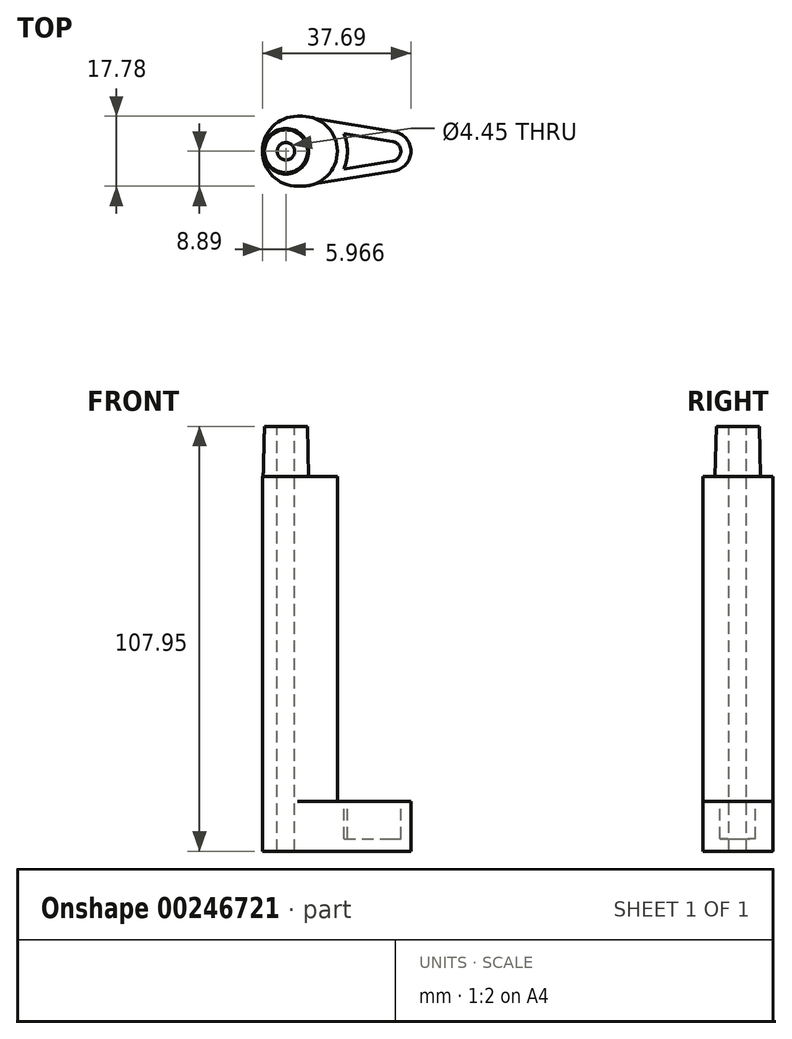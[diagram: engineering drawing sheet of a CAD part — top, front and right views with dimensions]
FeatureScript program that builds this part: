
annotation { "Feature Type Name" : "Feature", "Feature Type Description" : "" }
export const myFeature = defineFeature(function(context is Context, id is Id, definition is map)
    precondition{}
    {
        {
            var Q0;
            Q0=qCreatedBy(makeId("Top.planeOp"),FACE);
            var sketch = newSketch(context, id + "F0", { "sketchPlane" : qUnion([Q0])});
            skArc(sketch, "E0", {"start": v(-9.14, 8.77) * mm, "mid": v(-19.45, 0) * mm, "end": v(-9.14, -8.77) * mm});
            skArc(sketch, "E1", {"start": v(13.98, -5.01) * mm, "mid": v(18.24, 0) * mm, "end": v(13.98, 5.01) * mm});
            skLineSegment(sketch, "E2", {"start": v(-9.14, 8.77) * mm, "end": v(13.98, 5.01) * mm});
            skLineSegment(sketch, "E3", {"start": v(13.98, -5.01) * mm, "end": v(-9.14, -8.77) * mm});
            skSolve(sketch);
        }
        {
            var Q0;
            Q0=makeQuery(id+"F0.imprint","IMPRINT",FACE,{"disambiguationData":[TD([[makeQuery(id+"F0.imprint","IMPRINT",EDGE,{"derivedFrom":sQuery(id+"F0.wireOp",EDGE,"E0")}),1.0]])]});
            extrude(context, id + "F1", {"entities" : qUnion([Q0]), "depth" : 12.7 * mm});
        }
        {
            var Q0;
            Q0=makeQuery(id+"F1.opExtrude","CAP_FACE",FACE,{"disambiguationData":[OSD([sQuery(id+"F0.wireOp",EDGE,"E0"),sQuery(id+"F0.wireOp",EDGE,"E1"),sQuery(id+"F0.wireOp",EDGE,"E2"),sQuery(id+"F0.wireOp",EDGE,"E3")])],"isStart":false});
            var sketch = newSketch(context, id + "F2", { "sketchPlane" : qUnion([Q0])});
            skArc(sketch, "E4", {"start": v(-10.56, 8.9) * mm, "mid": v(-19.45, 0) * mm, "end": v(-10.56, -8.9) * mm});
            skArc(sketch, "E5", {"start": v(-9.3, -8.9) * mm, "mid": v(-0.4, 0) * mm, "end": v(-9.3, 8.9) * mm});
            skLineSegment(sketch, "E6", {"start": v(-10.56, 8.9) * mm, "end": v(-9.3, 8.9) * mm});
            skLineSegment(sketch, "E7", {"start": v(-10.56, -8.9) * mm, "end": v(-9.3, -8.9) * mm});
            skPoint(sketch, "E8.orphan", {"position": v(0, 8.9) * mm});
            skPoint(sketch, "E9.orphan", {"position": v(0, -8.9) * mm});
            skSolve(sketch);
        }
        {
            var Q0;
            Q0 = qSketchRegion(id + "F2", true);
            extrude(context, id + "F3", {"entities" : qUnion([Q0]), "operationType" : NewBodyOperationType.ADD, "depth" : 82.55 * mm});
        }
        {
            var Q0;
            Q0=qCreatedBy(makeId("Front.planeOp"),FACE);
            var sketch = newSketch(context, id + "F4", { "sketchPlane" : qUnion([Q0])});
            skLineSegment(sketch, "E10", {"start": v(-13.48, 0) * mm, "end": v(-13.48, 127) * mm});
            skSolve(sketch);
        }
        {
            var Q0;
            Q0=qCreatedBy(makeId("Front.planeOp"),FACE);
            var sketch = newSketch(context, id + "F5", { "sketchPlane" : qUnion([Q0])});
            skLineSegment(sketch, "E11", {"start": v(-7.7, 95.25) * mm, "end": v(-8.02, 107.95) * mm});
            skLineSegment(sketch, "E12", {"start": v(-8.02, 107.95) * mm, "end": v(-13.48, 107.95) * mm});
            skLineSegment(sketch, "E13", {"start": v(-13.48, 107.95) * mm, "end": v(-13.48, 95.25) * mm});
            skLineSegment(sketch, "E14", {"start": v(-13.48, 95.25) * mm, "end": v(-7.7, 95.25) * mm});
            skSolve(sketch);
        }
        {
            var Q0;
            Q0=makeQuery(id+"F5.imprint","IMPRINT",FACE,{"disambiguationData":[TD([[makeQuery(id+"F5.imprint","IMPRINT",EDGE,{"derivedFrom":sQuery(id+"F5.wireOp",EDGE,"E11")}),1.0]])]});
            var Q1;
            Q1=sQuery(id+"F4.wireOp",EDGE,"E10");
            revolve(context, id + "F6", {"operationType" : NewBodyOperationType.ADD, "entities" : qUnion([Q0]), "axis" : qUnion([Q1]), "revolveType" : RevolveType.FULL});
        }
        {
            var Q0;
            Q0=makeQuery(id+"F6.opRevolve","SWEPT_FACE",FACE,{"disambiguationData":[OSD([sQuery(id+"F5.wireOp",EDGE,"E12")])]});
            var sketch = newSketch(context, id + "F7", { "sketchPlane" : qUnion([Q0])});
            skCircle(sketch, "E15", {"center": v(-13.48, 0) * mm, "radius": 2.22 * mm});
            skSolve(sketch);
        }
        {
            var Q0;
            Q0=makeQuery(id+"F7.imprint","IMPRINT",FACE,{"disambiguationData":[TD([[makeQuery(id+"F7.imprint","IMPRINT",EDGE,{"derivedFrom":sQuery(id+"F7.wireOp",EDGE,"E15")}),1.0]])]});
            extrude(context, id + "F8", {"entities" : qUnion([Q0]), "operationType" : NewBodyOperationType.REMOVE, "endBound" : BoundingType.THROUGH_ALL, "oppositeDirection" : true, "depth" : 25.4 * mm});
        }
        {
            var Q0;
            Q0=makeQuery(id+"F1.opExtrude","CAP_FACE",FACE,{"disambiguationData":[OSD([sQuery(id+"F0.wireOp",EDGE,"E0"),sQuery(id+"F0.wireOp",EDGE,"E1"),sQuery(id+"F0.wireOp",EDGE,"E2"),sQuery(id+"F0.wireOp",EDGE,"E3")])],"isStart":false});
            var sketch = newSketch(context, id + "F9", { "sketchPlane" : qUnion([Q0])});
            skLineSegment(sketch, "E16.0", {"start": v(1.2, 4.52) * mm, "end": v(13.57, 2.5) * mm});
            skArc(sketch, "E16.1", {"start": v(1.2, -4.52) * mm, "mid": v(2.14, 0) * mm, "end": v(1.2, 4.52) * mm});
            skLineSegment(sketch, "E16.2", {"start": v(13.57, -2.5) * mm, "end": v(1.2, -4.52) * mm});
            skArc(sketch, "E16.3", {"start": v(13.57, -2.5) * mm, "mid": v(15.7, 0) * mm, "end": v(13.57, 2.5) * mm});
            skSolve(sketch);
        }
        {
            var Q0;
            Q0=makeQuery(id+"F9.imprint","IMPRINT",FACE,{"disambiguationData":[TD([[makeQuery(id+"F9.imprint","IMPRINT",EDGE,{"derivedFrom":sQuery(id+"F9.wireOp",EDGE,"E16.0")}),-1.0]])]});
            extrude(context, id + "F10", {"entities" : qUnion([Q0]), "operationType" : NewBodyOperationType.REMOVE, "oppositeDirection" : true, "depth" : 9.52 * mm});
        }
    });
